# Revit family: Switch-Lutron-Homeworks-QS_Vintage_Wired_Keypad new
name_source: partatom
category: Electrical Fixtures
units: mm (PartAtom-declared; Revit-internal decimal feet)

## family parameters
Cut with Voids When Loaded = Yes
Host = Face
Maintain Annotation Orientation = Yes
OmniClass Number = 23.85.80.11.27
OmniClass Title = Lighting Controls
Part Type = Switch
Room Calculation Point = No
Round Connector Dimension = Use Diameter
Shared = No

## types (12) — shared parameters
Additional Material Finish = Metal - Lutron - Aged Brass
Apparent Load = 0 VA
Assembly Code = D5030.50
Default Elevation = 0' - 0"
Description = HomeWorks QS Vintage Wired Keypad
Engraving Note = Engraving Options Available, Contact Manufacturer
Environment = Ambient operating temperature: 32 °F to 104 °F (0 °C to 40 °C),
0% to 90% non-condensing relative humidity. Indoor use only.
Instruction Sheet Link = Contact Manufacturer for Installation Documentation
Instruction Sheet Link - QS Keypad Base Unit = Contact Manufacturer for Installation Documentation
Keynote = 26 27 26
Load Classification = Other
Manufacturer = Lutron Electronics Co., Inc
Manufacturer Fax Number = 610-282-1243
Number of Poles = 1
Overall Depth = 0' - 3 9/16"
Performance URL = https://assets.lutron.com
Power Factor = 1
Product Documentation Link = https://assets.lutron.com
Product Name = QS Vintage Wired Keypad
Product Page URL = https://residential.lutron.com
Series = HomeWorks
URL = http://www.lutron.com
Version = 2020 - v1.0a
Video Link = https://www.youtube.com
Voltage = 24 V
Voltage Comment = 24-36V
Wallstation Material = Metal - Lutron - Aged Brass
Warranty URL = http://www.lutron.com
Wattage Comment = Contact Manufacturer for Wattage Information
zero-valued in all types: Cost

## per-type parameters (varying)
| type | C Back Box Height | C Back Box Width | Constraints | Model | Overall Height | Overall Width |
| QS Vintage Wired Keypad - 1 Gang - 1 Button - Standard | 0' - 2 11/16" | 0' - 2 11/16" | 1 | HW-AV-KP-S-1-T | 0' - 3 9/16" | 0' - 3 9/16" |
| QS Vintage Wired Keypad - 1 Gang - 2 Button - Standard | 0' - 2 11/16" | 0' - 2 11/16" | 3 | HW-AV-KP-S-11-TT | 0' - 3 9/16" | 0' - 3 9/16" |
| QS Vintage Wired Keypad - 1 Gang - 4 Button - Standard | 0' - 2 11/16" | 0' - 2 11/16" | 4 | HW-AV-KP-S-22-TTTT | 0' - 3 9/16" | 0' - 3 9/16" |
| QS Vintage Wired Keypad - 2 Gang - Horizontal - 3 Button - Standard | 0' - 2 11/16" | 0' - 5 5/16" | 7 | HW-AV-KP-H-111-TTT | 0' - 3 9/16" | 0' - 5 15/16" |
| QS Vintage Wired Keypad - 2 Gang - Horizontal - 4 Button - Standard | 0' - 2 11/16" | 0' - 5 5/16" | 8 | HW-AV-KP-H-1111-TTTT | 0' - 3 9/16" | 0' - 5 15/16" |
| QS Vintage Wired Keypad - 2 Gang - Vertical - 3 Button - Standard | 0' - 5 5/16" | 0' - 2 11/16" | 9 | HW-AV-KP-V-111-TTT | 0' - 5 15/16" | 0' - 3 9/16" |
| QS Vintage Wired Keypad - 1 Gang - 1 Button -  Engraved | 0' - 2 11/16" | 0' - 2 11/16" | 1 | HW-AV-KP-S-E-1-T | 0' - 3 9/16" | 0' - 3 9/16" |
| QS Vintage Wired Keypad - 1 Gang - 2 Button -  Engraved | 0' - 2 11/16" | 0' - 2 11/16" | 3 | HW-AV-KP-S-E-11-TT | 0' - 3 9/16" | 0' - 3 9/16" |
| QS Vintage Wired Keypad - 1 Gang - 4 Button -  Engraved | 0' - 2 11/16" | 0' - 2 11/16" | 4 | HW-AV-KP-S-E-22-TTTT | 0' - 3 9/16" | 0' - 3 9/16" |
| QS Vintage Wired Keypad - 2 Gang - Horizontal - 3 Button -  Engraved | 0' - 2 11/16" | 0' - 5 5/16" | 7 | HW-AV-KP-H-E-111-TTT | 0' - 3 9/16" | 0' - 5 15/16" |
| QS Vintage Wired Keypad - 2 Gang - Horizontal - 4 Button -  Engraved | 0' - 2 11/16" | 0' - 5 5/16" | 8 | HW-AV-KP-H-E-1111-TTTT | 0' - 3 9/16" | 0' - 5 15/16" |
| QS Vintage Wired Keypad - 2 Gang - Vertical - 3 Button -  Engraved | 0' - 5 5/16" | 0' - 2 11/16" | 9 | HW-AV-KP-V-E-111-TTT | 0' - 5 15/16" | 0' - 3 9/16" |

## geometry (parser evidence)
native form markers: Sweep x5
no freeform markers — native parametric forms only
